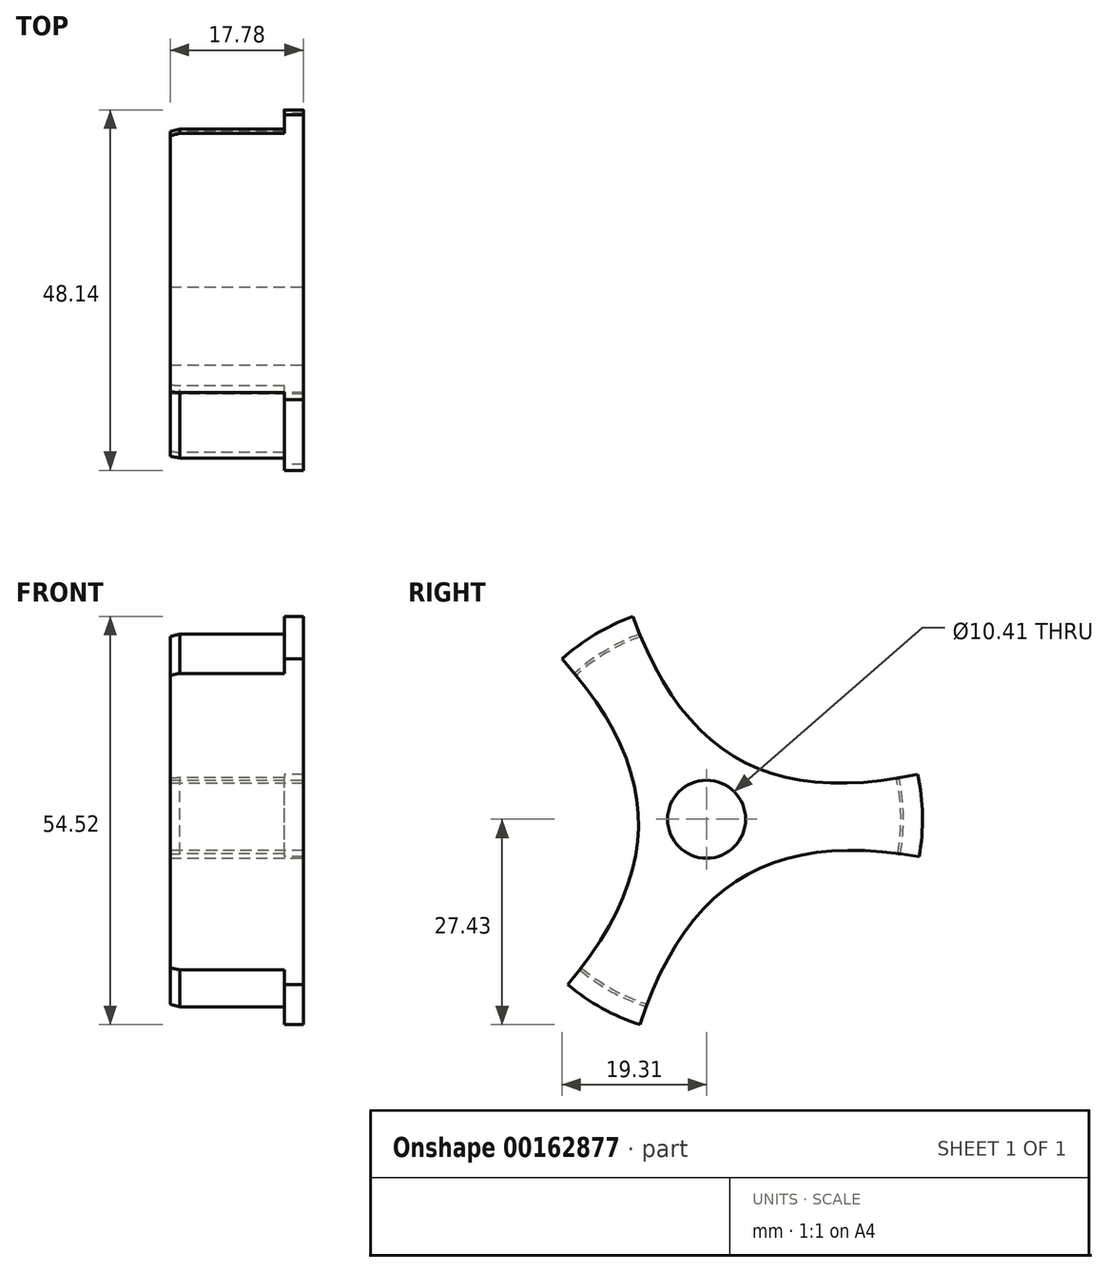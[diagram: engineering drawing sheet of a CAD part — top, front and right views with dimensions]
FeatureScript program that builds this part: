
annotation { "Feature Type Name" : "Feature", "Feature Type Description" : "" }
export const myFeature = defineFeature(function(context is Context, id is Id, definition is map)
    precondition{}
    {
        {
            var Q0;
            Q0=qCreatedBy(makeId("Right.planeOp"),FACE);
            var sketch = newSketch(context, id + "F0", { "sketchPlane" : qUnion([Q0])});
            skCircle(sketch, "E0", {"center": v(0, 0) * mm, "radius": 5.2 * mm});
            skCircle(sketch, "E1", {"center": v(0, 0) * mm, "radius": 26.29 * mm});
            skSolve(sketch);
        }
        {
            var Q0;
            Q0 = qSketchRegion(id + "F0", true);
            extrude(context, id + "F1", {"entities" : qUnion([Q0]), "oppositeDirection" : true, "depth" : 15.24 * mm});
        }
        {
            var Q0;
            Q0=makeQuery(id+"F1.opExtrude","CAP_FACE",FACE,{"disambiguationData":[OSD([sQuery(id+"F0.wireOp",EDGE,"E0"),sQuery(id+"F0.wireOp",EDGE,"E1")])],"isStart":true});
            var sketch = newSketch(context, id + "F2", { "sketchPlane" : qUnion([Q0])});
            skCircle(sketch, "E2", {"center": v(0, 0) * mm, "radius": 28.83 * mm});
            skCircle(sketch, "E3.0", {"center": v(0, 0) * mm, "radius": 5.2 * mm});
            skSolve(sketch);
        }
        {
            var Q0;
            Q0 = qSketchRegion(id + "F2", true);
            extrude(context, id + "F3", {"entities" : qUnion([Q0]), "operationType" : NewBodyOperationType.ADD, "depth" : 2.54 * mm});
        }
        {
            var Q0;
            Q0=makeQuery(id+"F1.opExtrude","CAP_FACE",FACE,{"disambiguationData":[OSD([sQuery(id+"F0.wireOp",EDGE,"E0"),sQuery(id+"F0.wireOp",EDGE,"E1")])],"isStart":false});
            var sketch = newSketch(context, id + "F4", { "sketchPlane" : qUnion([Q0])});
            skLineSegment(sketch, "E4", {"start": v(0, 0) * mm, "end": v(-53.81, 0) * mm, "construction": true});
            skLineSegment(sketch, "E5.1.0", {"start": v(0, 0) * mm, "end": v(26.9, -46.6) * mm, "construction": true});
            skLineSegment(sketch, "E5.2.0", {"start": v(0, 0) * mm, "end": v(26.9, 46.6) * mm, "construction": true});
            skPoint(sketch, "E5.center", {"position": v(0, 0) * mm});
            skLineSegment(sketch, "E6", {"start": v(0, 0) * mm, "end": v(-28.4, 5) * mm, "construction": true});
            skLineSegment(sketch, "E7.MirrorCS", {"start": v(0, 0) * mm, "end": v(-28.4, -5) * mm, "construction": true});
            skLineSegment(sketch, "E8", {"start": v(0, 0) * mm, "end": v(8.88, -27.43) * mm, "construction": true});
            skArc(sketch, "E9", {"start": v(7.18, -22.17) * mm, "mid": v(-12.01, -19.97) * mm, "end": v(-22.95, -4.05) * mm, "construction": true});
            skArc(sketch, "E10", {"start": v(5.55, -17.13) * mm, "mid": v(-11.82, -13.59) * mm, "end": v(-17.74, 3.13) * mm, "construction": true});
            skArc(sketch, "E11", {"start": v(4.5, -13.89) * mm, "mid": v(-10.87, -9.75) * mm, "end": v(-13.32, 5.98) * mm, "construction": true});
            skLineSegment(sketch, "E12", {"start": v(0, 0) * mm, "end": v(-13.32, 5.98) * mm, "construction": true});
            skCircle(sketch, "E13.0", {"center": v(0, 0) * mm, "radius": 28.83 * mm, "construction": true});
            skPoint(sketch, "E14.orphan", {"position": v(-39.83, -7.02) * mm});
            skPoint(sketch, "E15.orphan", {"position": v(-39.83, 7.02) * mm});
            skFitSpline(sketch, "E16", {"points": [v(8.88, -27.43) * mm, v(-28.4, -5) * mm], "startDerivative": vector(-18.43, 56.9) * mm, "endDerivative": vector(-58.9, -10.38) * mm});
            skCircle(sketch, "E17", {"center": v(0, 0) * mm, "radius": 8.9 * mm, "construction": true});
            skArc(sketch, "E18", {"start": v(-28.4, -5) * mm, "mid": v(-23.59, -39.21) * mm, "end": v(8.88, -27.43) * mm});
            skSolve(sketch);
        }
        {
            var Q0;
            {var subQ0=sQuery(id+"F4.wireOp",EDGE,"E18");Q0=makeQuery(id+"F4.imprint","IMPRINT",FACE,{"disambiguationData":[TD([[makeQuery(id+"F4.imprint","IMPRINT",EDGE,{"derivedFrom":subQ0}),1.0]])]});}
            var Q1;
            {var subQ0=sQuery(id+"F4.wireOp",EDGE,"E16");var subQ1=makeQuery(id+"F1.opExtrude","CAP_EDGE",EDGE,{"disambiguationData":[OSD([sQuery(id+"F0.wireOp",EDGE,"E1")])],"isStart":false});var subQ2=makeQuery(id+"F4.imprint","INTERSECT",VERTEX,{"disambiguationData":[OD(0.0)],"derivedFrom":[subQ1,subQ0]});Q1=makeQuery(id+"F4.imprint","IMPRINT",FACE,{"disambiguationData":[TD([[makeQuery(id+"F4.imprint","IMPRINT",EDGE,{"disambiguationData":[TD([[subQ2,-1.0]])],"derivedFrom":subQ0}),1.0]])]});}
            extrude(context, id + "F5", {"entities" : qUnion([Q0, Q1]), "endBound" : BoundingType.THROUGH_ALL, "oppositeDirection" : true, "depth" : 25.4 * mm});
        }
        {
            var Q0;
            Q0=makeQuery(id+"F5.opExtrude","SWEPT_BODY",BODY,{"disambiguationData":[OSD([sQuery(id+"F4.wireOp",EDGE,"E16"),sQuery(id+"F4.wireOp",EDGE,"E18")])]});
            var Q1;
            Q1=makeQuery(id+"F1.opExtrude","SWEPT_FACE",FACE,{"disambiguationData":[OSD([sQuery(id+"F0.wireOp",EDGE,"E1")])]});
            circularPattern(context, id + "F6", {"entities" : qUnion([Q0]), "axis" : qUnion([Q1]), "angle" : 120 * degree, "instanceCount" : 3});
        }
        {
            var Q0;
            Q0=makeQuery(id+"F5.opExtrude","SWEPT_BODY",BODY,{"disambiguationData":[OSD([sQuery(id+"F4.wireOp",EDGE,"E16"),sQuery(id+"F4.wireOp",EDGE,"E18")])]});
            var Q1;
            Q1=makeQuery(id+"F6.opPattern","COPY",BODY,{"derivedFrom":makeQuery(id+"F5.opExtrude","SWEPT_BODY",BODY,{"disambiguationData":[OSD([sQuery(id+"F4.wireOp",EDGE,"E16"),sQuery(id+"F4.wireOp",EDGE,"E18")])]}),"instanceName":"2"});
            var Q2;
            Q2=makeQuery(id+"F6.opPattern","COPY",BODY,{"derivedFrom":makeQuery(id+"F5.opExtrude","SWEPT_BODY",BODY,{"disambiguationData":[OSD([sQuery(id+"F4.wireOp",EDGE,"E16"),sQuery(id+"F4.wireOp",EDGE,"E18")])]}),"instanceName":"1"});
            var Q3;
            Q3=makeQuery(id+"F1.opExtrude","SWEPT_BODY",BODY,{"disambiguationData":[OSD([sQuery(id+"F0.wireOp",EDGE,"E0"),sQuery(id+"F0.wireOp",EDGE,"E1")])]});
            booleanBodies(context, id + "F7", {"operationType" : BooleanOperationType.SUBTRACTION, "tools" : qUnion([Q0, Q1, Q2]), "targets" : qUnion([Q3])});
        }
        {
            var Q0;
            {var subQ0=sQuery(id+"F0.wireOp",EDGE,"E1");var subQ1=makeQuery(id+"F5.opExtrude","SWEPT_FACE",FACE,{"disambiguationData":[OSD([sQuery(id+"F4.wireOp",EDGE,"E16")])]});Q0=makeQuery(id+"F7.opBoolean","SPLIT",EDGE,{"disambiguationData":[TD([makeQuery(id+"F1.opExtrude","CAP_FACE",FACE,{"disambiguationData":[OSD([sQuery(id+"F0.wireOp",EDGE,"E0"),subQ0])],"isStart":false}),makeQuery(id+"F1.opExtrude","SWEPT_FACE",FACE,{"disambiguationData":[OSD([subQ0])]}),subQ1,makeQuery(id+"F6.opPattern","COPY",FACE,{"derivedFrom":subQ1,"instanceName":"1"})])],"derivedFrom":makeQuery(id+"F1.opExtrude","CAP_EDGE",EDGE,{"disambiguationData":[OSD([subQ0])],"isStart":false})});}
            var Q1;
            {var subQ0=sQuery(id+"F0.wireOp",EDGE,"E1");var subQ1=makeQuery(id+"F5.opExtrude","SWEPT_FACE",FACE,{"disambiguationData":[OSD([sQuery(id+"F4.wireOp",EDGE,"E16")])]});Q1=makeQuery(id+"F7.opBoolean","SPLIT",EDGE,{"disambiguationData":[TD([makeQuery(id+"F1.opExtrude","CAP_FACE",FACE,{"disambiguationData":[OSD([sQuery(id+"F0.wireOp",EDGE,"E0"),subQ0])],"isStart":false}),makeQuery(id+"F1.opExtrude","SWEPT_FACE",FACE,{"disambiguationData":[OSD([subQ0])]}),makeQuery(id+"F6.opPattern","COPY",FACE,{"derivedFrom":subQ1,"instanceName":"1"}),makeQuery(id+"F6.opPattern","COPY",FACE,{"derivedFrom":subQ1,"instanceName":"2"})])],"derivedFrom":makeQuery(id+"F1.opExtrude","CAP_EDGE",EDGE,{"disambiguationData":[OSD([subQ0])],"isStart":false})});}
            var Q2;
            {var subQ0=sQuery(id+"F0.wireOp",EDGE,"E1");var subQ1=makeQuery(id+"F5.opExtrude","SWEPT_FACE",FACE,{"disambiguationData":[OSD([sQuery(id+"F4.wireOp",EDGE,"E16")])]});Q2=makeQuery(id+"F7.opBoolean","SPLIT",EDGE,{"disambiguationData":[TD([makeQuery(id+"F1.opExtrude","CAP_FACE",FACE,{"disambiguationData":[OSD([sQuery(id+"F0.wireOp",EDGE,"E0"),subQ0])],"isStart":false}),makeQuery(id+"F1.opExtrude","SWEPT_FACE",FACE,{"disambiguationData":[OSD([subQ0])]}),subQ1,makeQuery(id+"F6.opPattern","COPY",FACE,{"derivedFrom":subQ1,"instanceName":"2"})])],"derivedFrom":makeQuery(id+"F1.opExtrude","CAP_EDGE",EDGE,{"disambiguationData":[OSD([subQ0])],"isStart":false})});}
            chamfer(context, id + "F8", {"entities" : qUnion([Q0, Q1, Q2]), "chamferType" : ChamferType.OFFSET_ANGLE, "width" : 1.27 * mm, "oppositeDirection" : false, "angle" : 15 * degree, "tangentPropagation" : true});
        }
    });
